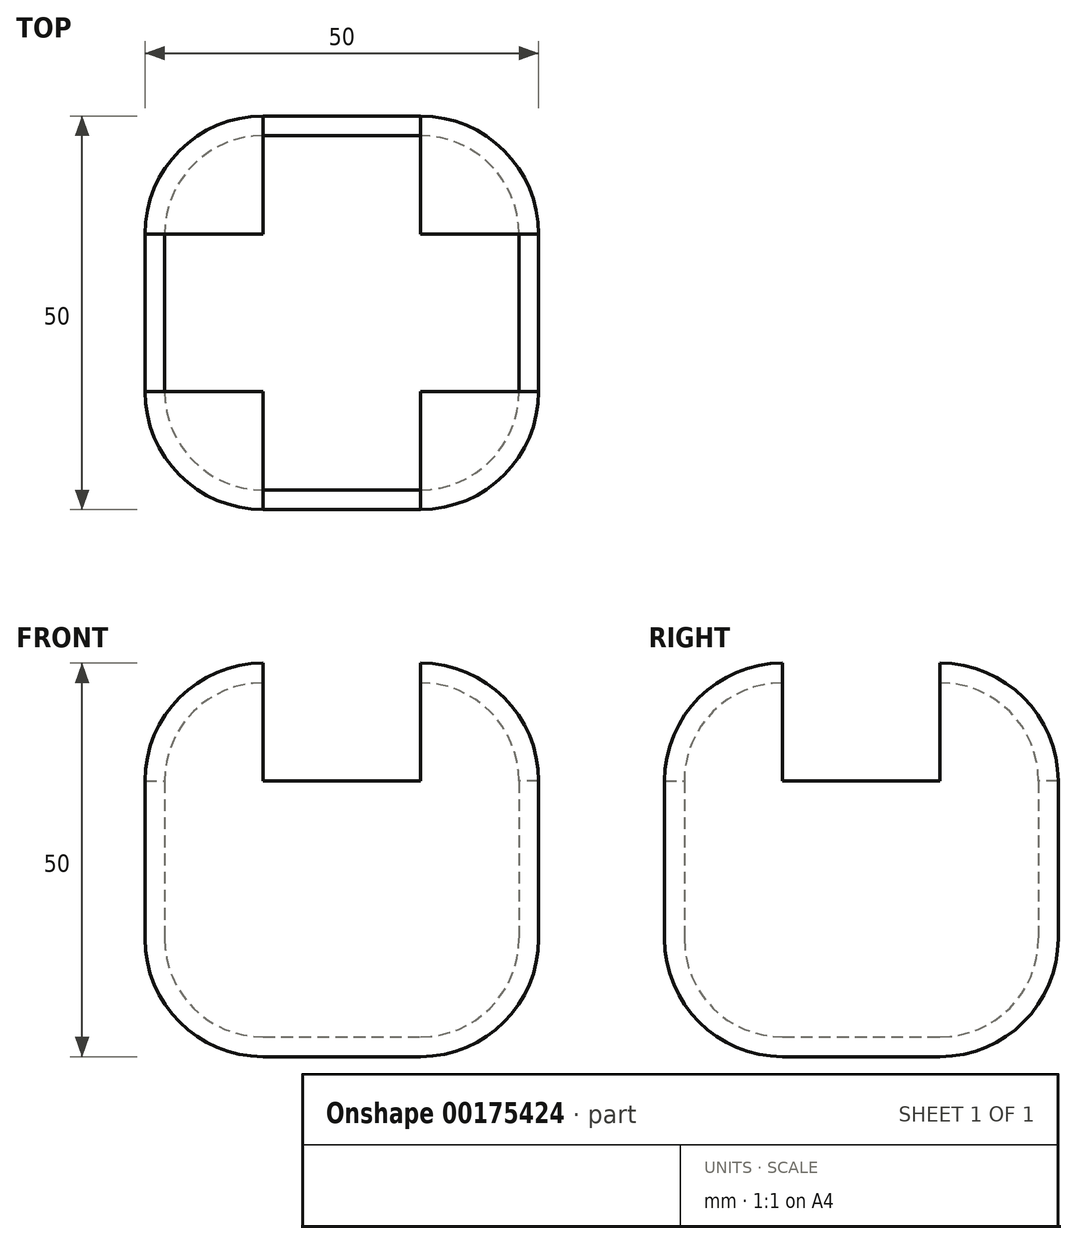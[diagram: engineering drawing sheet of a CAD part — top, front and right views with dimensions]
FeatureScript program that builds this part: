
annotation { "Feature Type Name" : "Feature", "Feature Type Description" : "" }
export const myFeature = defineFeature(function(context is Context, id is Id, definition is map)
    precondition{}
    {
        {
            var Q0;
            Q0=qCreatedBy(makeId("Top.planeOp"),FACE);
            var sketch = newSketch(context, id + "F0", { "sketchPlane" : qUnion([Q0])});
            skLineSegment(sketch, "E0.bottom", {"start": v(25, 25) * mm, "end": v(-25, 25) * mm});
            skLineSegment(sketch, "E0.top", {"start": v(25, -25) * mm, "end": v(-25, -25) * mm});
            skLineSegment(sketch, "E0.left", {"start": v(25, 25) * mm, "end": v(25, -25) * mm});
            skLineSegment(sketch, "E0.right", {"start": v(-25, 25) * mm, "end": v(-25, -25) * mm});
            skPoint(sketch, "E0.middle", {"position": v(0, 0) * mm});
            skSolve(sketch);
        }
        {
            var Q0;
            Q0=makeQuery(id+"F0.imprint","IMPRINT",FACE,{"disambiguationData":[TD([[makeQuery(id+"F0.imprint","IMPRINT",EDGE,{"derivedFrom":sQuery(id+"F0.wireOp",EDGE,"E0.bottom")}),1.0]])]});
            extrude(context, id + "F1", {"entities" : qUnion([Q0]), "endBound" : BoundingType.SYMMETRIC, "depth" : 50 * mm});
        }
        {
            var Q0;
            Q0=makeQuery(id+"F1.opExtrude","CAP_EDGE",EDGE,{"disambiguationData":[OSD([sQuery(id+"F0.wireOp",EDGE,"E0.right")])],"isStart":false});
            fillet(context, id + "F2", {"entities" : qUnion([Q0]), "radius" : 15 * mm, "tangentPropagation" : true, "allowEdgeOverflow" : false});
        }
        {
            var Q0;
            Q0=makeQuery(id+"F1.opExtrude","CAP_EDGE",EDGE,{"disambiguationData":[OSD([sQuery(id+"F0.wireOp",EDGE,"E0.top")])],"isStart":false});
            fillet(context, id + "F3", {"entities" : qUnion([Q0]), "radius" : 15 * mm, "tangentPropagation" : true, "allowEdgeOverflow" : false});
        }
        {
            var Q0;
            Q0=makeQuery(id+"F1.opExtrude","CAP_EDGE",EDGE,{"disambiguationData":[OSD([sQuery(id+"F0.wireOp",EDGE,"E0.left")])],"isStart":false});
            fillet(context, id + "F4", {"entities" : qUnion([Q0]), "radius" : 15 * mm, "tangentPropagation" : true, "allowEdgeOverflow" : false});
        }
        {
            var Q0;
            Q0=makeQuery(id+"F1.opExtrude","CAP_EDGE",EDGE,{"disambiguationData":[OSD([sQuery(id+"F0.wireOp",EDGE,"E0.bottom")])],"isStart":false});
            fillet(context, id + "F5", {"entities" : qUnion([Q0]), "radius" : 15 * mm, "tangentPropagation" : true, "allowEdgeOverflow" : false});
        }
        {
            var Q0;
            Q0=makeQuery(id+"F1.opExtrude","CAP_EDGE",EDGE,{"disambiguationData":[OSD([sQuery(id+"F0.wireOp",EDGE,"E0.left")])],"isStart":true});
            fillet(context, id + "F6", {"entities" : qUnion([Q0]), "radius" : 15 * mm, "tangentPropagation" : true, "allowEdgeOverflow" : false});
        }
        {
            var Q0;
            Q0=makeQuery(id+"F1.opExtrude","CAP_FACE",FACE,{"disambiguationData":[OSD([sQuery(id+"F0.wireOp",EDGE,"E0.bottom"),sQuery(id+"F0.wireOp",EDGE,"E0.top"),sQuery(id+"F0.wireOp",EDGE,"E0.left"),sQuery(id+"F0.wireOp",EDGE,"E0.right")])],"isStart":false});
            var Q1;
            Q1=makeQuery(id+"F2.opFillet","BLEND_FACE",FACE,{"disambiguationData":[OSD([sQuery(id+"F0.wireOp",EDGE,"E0.right")])]});
            var Q2;
            Q2=makeQuery(id+"F5.opFillet","BLEND_FACE",FACE,{"disambiguationData":[OSD([sQuery(id+"F0.wireOp",EDGE,"E0.bottom")])]});
            var Q3;
            Q3=makeQuery(id+"F4.opFillet","BLEND_FACE",FACE,{"disambiguationData":[OSD([sQuery(id+"F0.wireOp",EDGE,"E0.left")])]});
            var Q4;
            Q4=makeQuery(id+"F3.opFillet","BLEND_FACE",FACE,{"disambiguationData":[OSD([sQuery(id+"F0.wireOp",EDGE,"E0.top")])]});
            shell(context, id + "F7", {"entities" : qUnion([Q0, Q1, Q2, Q3, Q4]), "thickness" : 2.5 * mm});
        }
    });
